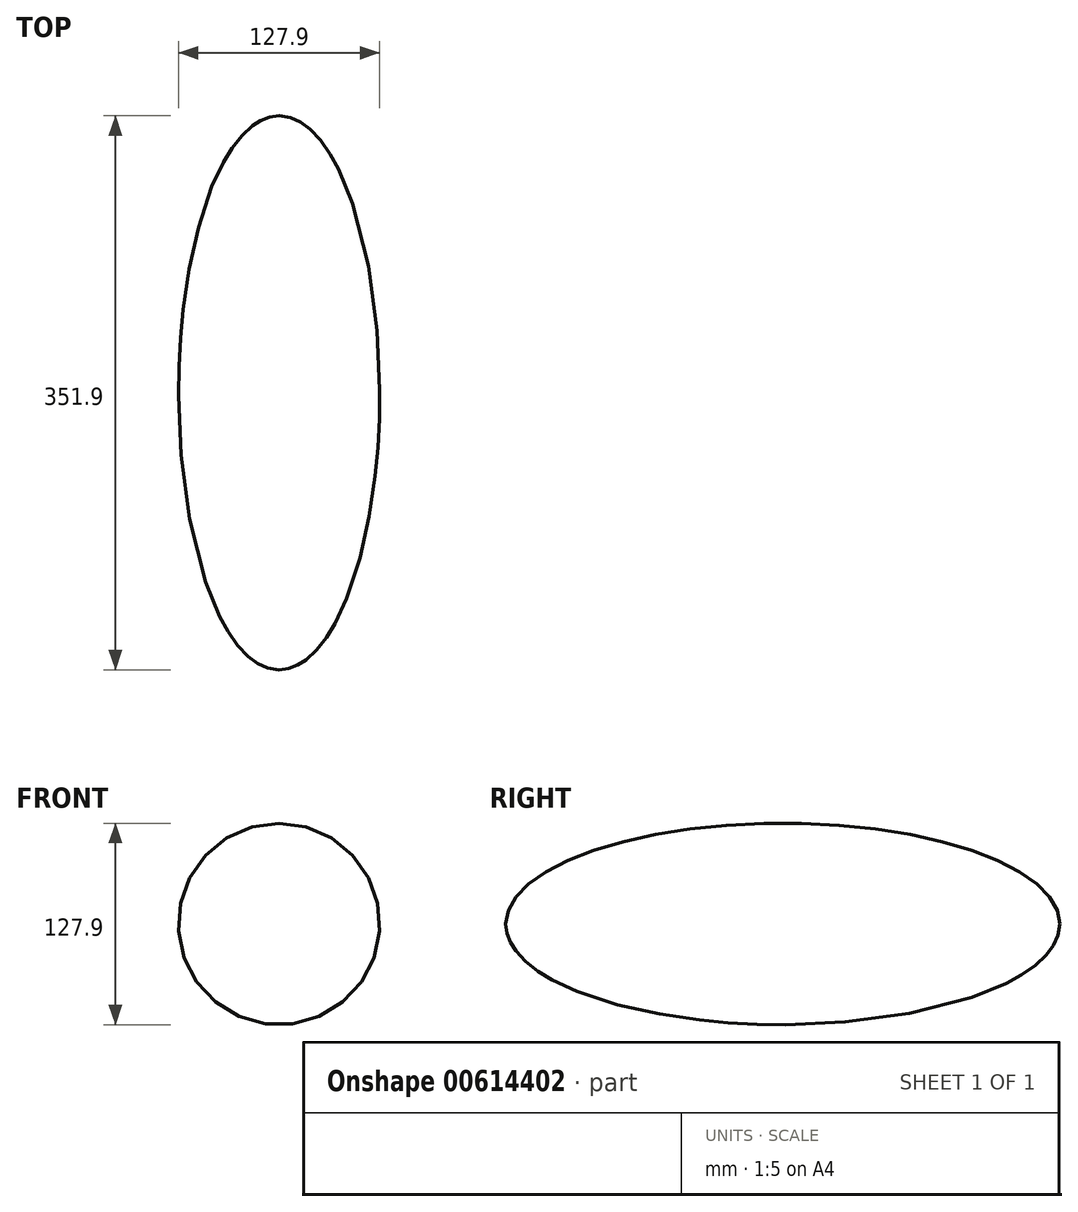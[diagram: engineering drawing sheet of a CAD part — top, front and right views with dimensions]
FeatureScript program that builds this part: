
annotation { "Feature Type Name" : "Feature", "Feature Type Description" : "" }
export const myFeature = defineFeature(function(context is Context, id is Id, definition is map)
    precondition{}
    {
        {
            var Q0;
            Q0=qCreatedBy(makeId("Right.planeOp"),FACE);
            var sketch = newSketch(context, id + "F0", { "sketchPlane" : qUnion([Q0])});
            skEllipticalArc(sketch, "E0", {});
            skLineSegment(sketch, "E1", {"start": v(-175.95, 0) * mm, "end": v(175.95, 0) * mm});
            const initialGuessF0  = {"E0": [0, 0, 1, 0, 0.17594990134239197, 0.06394925942408307, 0, 3.141592653589793]};
            skSetInitialGuess(sketch, initialGuessF0);
            skSolve(sketch);
        }
        {
            var Q0;
            Q0=makeQuery(id+"F0.imprint","IMPRINT",FACE,{"disambiguationData":[TD([[makeQuery(id+"F0.imprint","IMPRINT",EDGE,{"derivedFrom":sQuery(id+"F0.wireOp",EDGE,"E0")}),1.0]])]});
            var Q1;
            Q1=sQuery(id+"F0.wireOp",EDGE,"E1");
            revolve(context, id + "F1", {"entities" : qUnion([Q0]), "axis" : qUnion([Q1]), "revolveType" : RevolveType.FULL});
        }
    });
